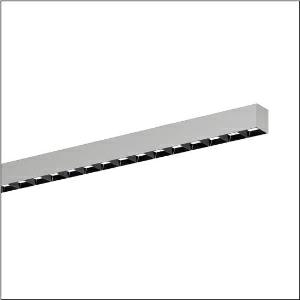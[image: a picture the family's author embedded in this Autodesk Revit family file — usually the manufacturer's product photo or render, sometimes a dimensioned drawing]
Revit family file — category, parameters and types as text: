
# Revit family: silica_r__21_51mx22tat4s_f26d
name_source: partatom
category: Lighting Fixtures
units: mm (PartAtom-declared; Revit-internal decimal feet)

## family parameters
Cut with Voids When Loaded = No
Host = Face
Light Source = No
Part Type = Normal
Room Calculation Point = No
Round Connector Dimension = Use Diameter
Shared = No

## types (1)
- --- (1 x LED, 3720 lm, 32.1 W, 6500K)
    Apparent Load = 32 VA
    CIE Flux Codes = 84 100 100 100 100
    Color Rendering = 80
    Color Temperature = 6500K
    Default Elevation = 1800 mm
    Description = Silica® 21, office luminaire, primary light control with darklight reflector, of PMMA, black, CAT 2 (L<= 3000cd/m²), light emission: direct distribution, primary light characteristic: symmetric, installation type: surface-mounted, LED, rated luminous flux: 3.720lm, luminous efficacy: 110lm/W, light colour: 8tw, colour temperature: 2700..6500K, control gear: ECG DALI, with terminal, 3+2-pole, max. 2.5mm², mains connection: 220..240V, AC, 50/60Hz, rated input power: 33.8W, luminaire housing, of aluminium, metallic grey (RAL 9006), length: 1.204mm, width: 53mm, height: 53mm, protection rating (complete): IP20, insulation class (complete): insulation class I (protective earthing), certification: CE, permissible operating ambient temperature: 0..+35°C, standard: EN 50419, packaging unit: 1 piece
    Height = 0 mm  [stored 0 ft]
    Lamp = 1 x LED
    Lamp Light Flux = 3720 lm
    Lamp Power = 32.1 W
    Lamp count = 1
    Length = 1204 mm
    Luminous efficacy = 116 lm/W
    Manufacturer = Siteco
    ModVariant = No
    Model = 51MX22TAT4S
    Mounting Place = Ceiling
    Mounting Type = Recessed
    Number of Poles = 1
    OnlyDefault = Yes
    Power Factor = 1
    Product Name = Silica® 21
    Product group = office luminaire | ceiling recessed
    ProductGroupID = 401
    Protection Class = Protection class I
    Protection Degree = IP 20
    RLX_Detail_Level = 1
    RLX_Emergency_Light_Flux = 0 lm
    RLX_Emergency_Type = 0
    RLX_Emergency_Type_DB = No
    RlxData = <blob elided: 39389 chars, md5=9f1d875f>
    Socket = socket
    Standby Power = 0 W
    System Light Flux = 3720 lm
    System Power = 32 W
    Type Comments = individual setting
    Type Image = l_1297764.jpg
    URL = http://relux.com
    VarID = @adj_071449
    Voltage = 0 V
    Weight = 0.00 kg
    Width = 53 mm

note: [stored X ft] marks values corroborated as IEEE doubles in the binary element streams (Revit-internal decimal feet)

## geometry (parser evidence)
native form markers: Blend x4, Sweep x11
no freeform markers — native parametric forms only
